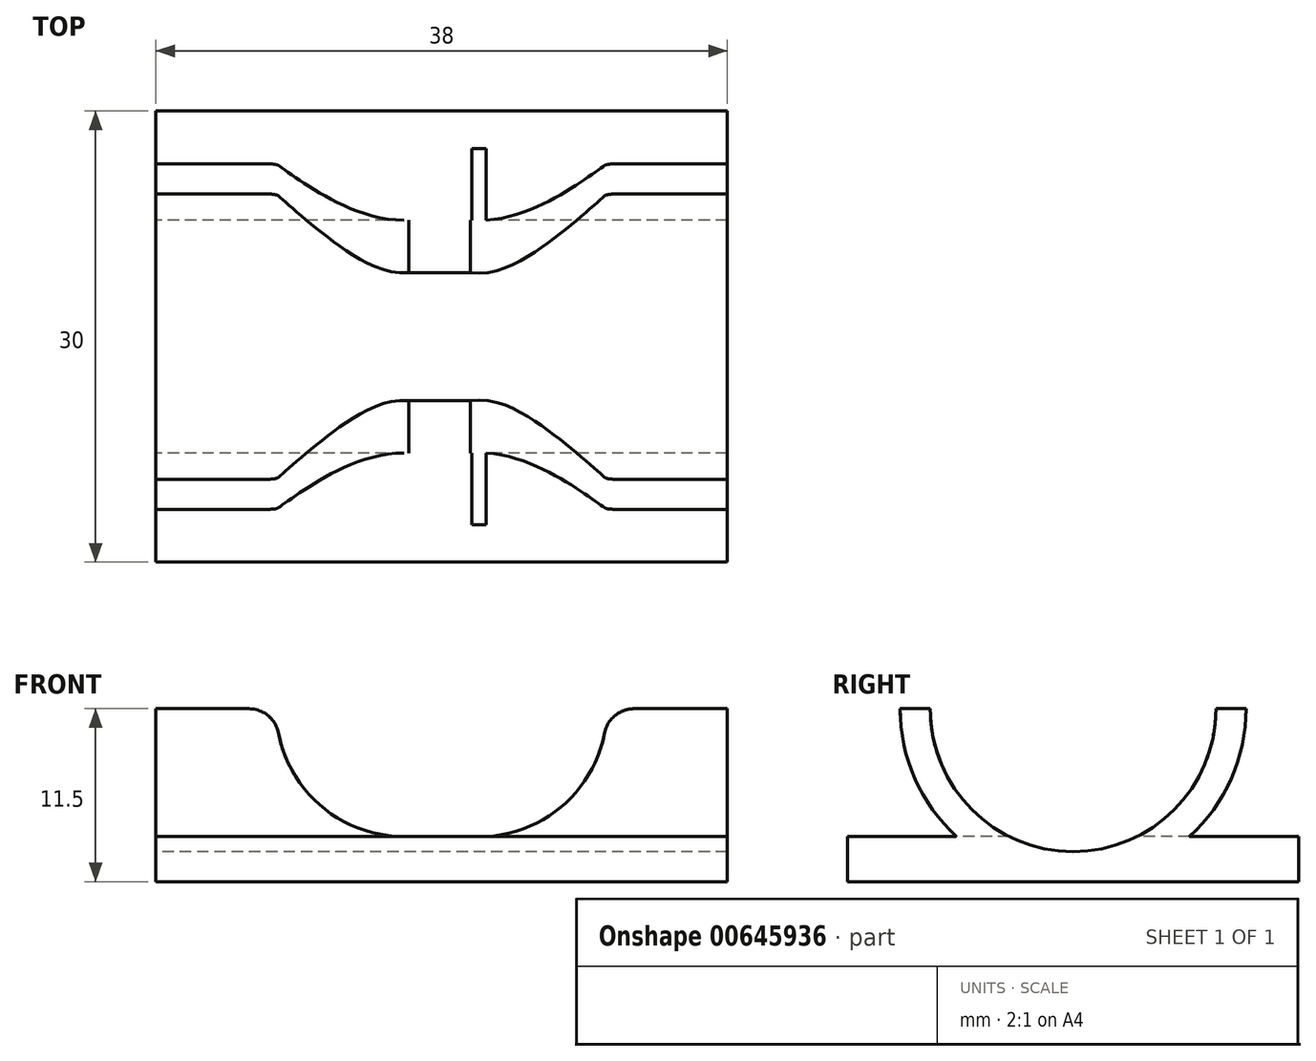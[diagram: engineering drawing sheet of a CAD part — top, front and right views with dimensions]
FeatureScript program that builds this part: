
annotation { "Feature Type Name" : "Feature", "Feature Type Description" : "" }
export const myFeature = defineFeature(function(context is Context, id is Id, definition is map)
    precondition{}
    {
        {
            var Q0;
            Q0=qCreatedBy(makeId("Front.planeOp"),FACE);
            var sketch = newSketch(context, id + "F0", { "sketchPlane" : qUnion([Q0])});
            skLineSegment(sketch, "E0", {"start": v(-54.5, 0) * mm, "end": v(60.13, 0) * mm, "construction": true});
            skLineSegment(sketch, "E1", {"start": v(-6.1, 9.5) * mm, "end": v(9.9, 9.5) * mm});
            skLineSegment(sketch, "E2", {"start": v(9.9, 9.5) * mm, "end": v(9.9, 9.5) * mm});
            skLineSegment(sketch, "E3", {"start": v(9.9, 9.5) * mm, "end": v(21.9, 9.5) * mm});
            skLineSegment(sketch, "E4", {"start": v(21.9, 11.5) * mm, "end": v(-16.1, 11.5) * mm});
            skLineSegment(sketch, "E5", {"start": v(-16.1, 11.5) * mm, "end": v(-16.1, 9.5) * mm});
            skLineSegment(sketch, "E6", {"start": v(-16.1, 9.5) * mm, "end": v(-6.1, 9.5) * mm});
            skLineSegment(sketch, "E7", {"start": v(-6.1, 9.5) * mm, "end": v(-6.1, 9.5) * mm});
            skLineSegment(sketch, "E8", {"start": v(21.9, 9.5) * mm, "end": v(21.9, 11.5) * mm});
            skSolve(sketch);
        }
        {
            var Q0;
            Q0=makeQuery(id+"F0.imprint","IMPRINT",FACE,{"disambiguationData":[TD([[makeQuery(id+"F0.imprint","IMPRINT",EDGE,{"derivedFrom":sQuery(id+"F0.wireOp",EDGE,"E1")}),1.0]])]});
            var Q1;
            Q1=sQuery(id+"F0.wireOp",EDGE,"E0");
            revolve(context, id + "F1", {"entities" : qUnion([Q0]), "axis" : qUnion([Q1]), "revolveType" : RevolveType.FULL});
        }
        {
            var Q0;
            Q0=makeQuery(id+"F1.opRevolve","SWEPT_FACE",FACE,{"disambiguationData":[OSD([sQuery(id+"F0.wireOp",EDGE,"E8")])]});
            var sketch = newSketch(context, id + "F2", { "sketchPlane" : qUnion([Q0])});
            skLineSegment(sketch, "E9.bottom", {"start": v(0, -11.5) * mm, "end": v(15, -11.5) * mm});
            skLineSegment(sketch, "E9.top", {"start": v(0, -8.5) * mm, "end": v(15, -8.5) * mm});
            skLineSegment(sketch, "E9.left", {"start": v(0, -11.5) * mm, "end": v(0, -8.5) * mm});
            skLineSegment(sketch, "E9.right", {"start": v(15, -11.5) * mm, "end": v(15, -8.5) * mm});
            skLineSegment(sketch, "E10.MirrorCS", {"start": v(-15, -11.5) * mm, "end": v(-15, -8.5) * mm});
            skLineSegment(sketch, "E11.MirrorCS", {"start": v(0, -8.5) * mm, "end": v(-15, -8.5) * mm});
            skLineSegment(sketch, "E12.MirrorCS", {"start": v(0, -11.5) * mm, "end": v(-15, -11.5) * mm});
            skSolve(sketch);
        }
        {
            var Q0;
            {var subQ0=sQuery(id+"F2.wireOp",EDGE,"E10.MirrorCS");Q0=makeQuery(id+"F2.imprint","IMPRINT",FACE,{"disambiguationData":[TD([[makeQuery(id+"F2.imprint","IMPRINT",EDGE,{"derivedFrom":subQ0}),-1.0]])]});}
            var Q1;
            {var subQ0=sQuery(id+"F2.wireOp",EDGE,"E9.bottom");Q1=makeQuery(id+"F2.imprint","IMPRINT",FACE,{"disambiguationData":[TD([[makeQuery(id+"F2.imprint","IMPRINT",EDGE,{"derivedFrom":subQ0}),1.0]])]});}
            var Q2;
            Q2=makeQuery(id+"F1.opRevolve","SWEPT_FACE",FACE,{"disambiguationData":[OSD([sQuery(id+"F0.wireOp",EDGE,"E5")])]});
            extrude(context, id + "F3", {"entities" : qUnion([Q0, Q1]), "operationType" : NewBodyOperationType.ADD, "endBound" : BoundingType.UP_TO_SURFACE, "oppositeDirection" : true, "depth" : 25 * mm, "endBoundEntityFace" : qUnion([Q2]), "offsetDistance" : 25 * mm});
        }
        {
            var Q0;
            {var subQ0=sQuery(id+"F0.wireOp",EDGE,"E8");var subQ1=sQuery(id+"F0.wireOp",EDGE,"E4");Q0=makeQuery(id+"F3.boolean.opBoolean","MERGE",FACE,{"derivedFrom":[makeQuery(id+"F1.opRevolve","SWEPT_FACE",FACE,{"disambiguationData":[OSD([subQ0])]}),makeQuery(id+"F3.opExtrude","CAP_FACE",FACE,{"disambiguationData":[OSD([subQ1,subQ0,sQuery(id+"F2.wireOp",EDGE,"E9.bottom"),sQuery(id+"F2.wireOp",EDGE,"E9.top"),sQuery(id+"F2.wireOp",EDGE,"E9.right")])],"isStart":true}),makeQuery(id+"F3.opExtrude","CAP_FACE",FACE,{"disambiguationData":[OSD([subQ1,subQ0,sQuery(id+"F2.wireOp",EDGE,"E10.MirrorCS"),sQuery(id+"F2.wireOp",EDGE,"E11.MirrorCS"),sQuery(id+"F2.wireOp",EDGE,"E12.MirrorCS")])],"isStart":true})]});}
            var sketch = newSketch(context, id + "F4", { "sketchPlane" : qUnion([Q0])});
            skLineSegment(sketch, "E13.bottom", {"start": v(-14.18, 0) * mm, "end": v(14.92, 0) * mm});
            skLineSegment(sketch, "E13.top", {"start": v(-14.18, 15.47) * mm, "end": v(14.92, 15.47) * mm});
            skLineSegment(sketch, "E13.left", {"start": v(-14.18, 0) * mm, "end": v(-14.18, 15.47) * mm});
            skLineSegment(sketch, "E13.right", {"start": v(14.92, 0) * mm, "end": v(14.92, 15.47) * mm});
            skSolve(sketch);
        }
        {
            var Q0;
            Q0 = qSketchRegion(id + "F4", true);
            extrude(context, id + "F5", {"entities" : qUnion([Q0]), "operationType" : NewBodyOperationType.REMOVE, "endBound" : BoundingType.THROUGH_ALL, "oppositeDirection" : true, "depth" : 25 * mm, "offsetDistance" : 25 * mm});
        }
        {
            var Q0;
            Q0=qCreatedBy(makeId("Front.planeOp"),FACE);
            var sketch = newSketch(context, id + "F6", { "sketchPlane" : qUnion([Q0])});
            skCircle(sketch, "E14", {"center": v(0.4, 0) * mm, "radius": 8.5 * mm});
            skCircle(sketch, "E15", {"center": v(5.4, -0.01) * mm, "radius": 8.5 * mm});
            skLineSegment(sketch, "E16", {"start": v(0.1, -8.5) * mm, "end": v(5.98, -8.5) * mm});
            skSolve(sketch);
        }
        {
            var Q0;
            Q0 = qSketchRegion(id + "F6", true);
            extrude(context, id + "F7", {"entities" : qUnion([Q0]), "operationType" : NewBodyOperationType.REMOVE, "endBound" : BoundingType.SYMMETRIC, "oppositeDirection" : true, "depth" : 25 * mm, "offsetDistance" : 25 * mm});
        }
        {
            var Q0;
            Q0=makeQuery(id+"F7.boolean.opBoolean","INTERSECT",EDGE,{"derivedFrom":[makeQuery(id+"F5.boolean.opBoolean","COPY",FACE,{"disambiguationData":[OD(0.0)],"derivedFrom":makeQuery(id+"F5.opExtrude","SWEPT_FACE",FACE,{"disambiguationData":[OSD([sQuery(id+"F4.wireOp",EDGE,"E13.bottom")])]})}),makeQuery(id+"F7.opExtrude","SWEPT_FACE",FACE,{"disambiguationData":[OSD([sQuery(id+"F6.wireOp",EDGE,"E14")])]})]});
            var Q1;
            Q1=makeQuery(id+"F7.boolean.opBoolean","INTERSECT",EDGE,{"derivedFrom":[makeQuery(id+"F5.boolean.opBoolean","COPY",FACE,{"disambiguationData":[OD(1.0)],"derivedFrom":makeQuery(id+"F5.opExtrude","SWEPT_FACE",FACE,{"disambiguationData":[OSD([sQuery(id+"F4.wireOp",EDGE,"E13.bottom")])]})}),makeQuery(id+"F7.opExtrude","SWEPT_FACE",FACE,{"disambiguationData":[OSD([sQuery(id+"F6.wireOp",EDGE,"E14")])]})]});
            var Q2;
            Q2=makeQuery(id+"F7.boolean.opBoolean","INTERSECT",EDGE,{"derivedFrom":[makeQuery(id+"F5.boolean.opBoolean","COPY",FACE,{"disambiguationData":[OD(1.0)],"derivedFrom":makeQuery(id+"F5.opExtrude","SWEPT_FACE",FACE,{"disambiguationData":[OSD([sQuery(id+"F4.wireOp",EDGE,"E13.bottom")])]})}),makeQuery(id+"F7.opExtrude","SWEPT_FACE",FACE,{"disambiguationData":[OSD([sQuery(id+"F6.wireOp",EDGE,"E15")])]})]});
            var Q3;
            Q3=makeQuery(id+"F7.boolean.opBoolean","INTERSECT",EDGE,{"derivedFrom":[makeQuery(id+"F5.boolean.opBoolean","COPY",FACE,{"disambiguationData":[OD(0.0)],"derivedFrom":makeQuery(id+"F5.opExtrude","SWEPT_FACE",FACE,{"disambiguationData":[OSD([sQuery(id+"F4.wireOp",EDGE,"E13.bottom")])]})}),makeQuery(id+"F7.opExtrude","SWEPT_FACE",FACE,{"disambiguationData":[OSD([sQuery(id+"F6.wireOp",EDGE,"E15")])]})]});
            fillet(context, id + "F8", {"entities" : qUnion([Q0, Q1, Q2, Q3]), "radius" : 2 * mm, "tangentPropagation" : true, "allowEdgeOverflow" : false});
        }
    });
